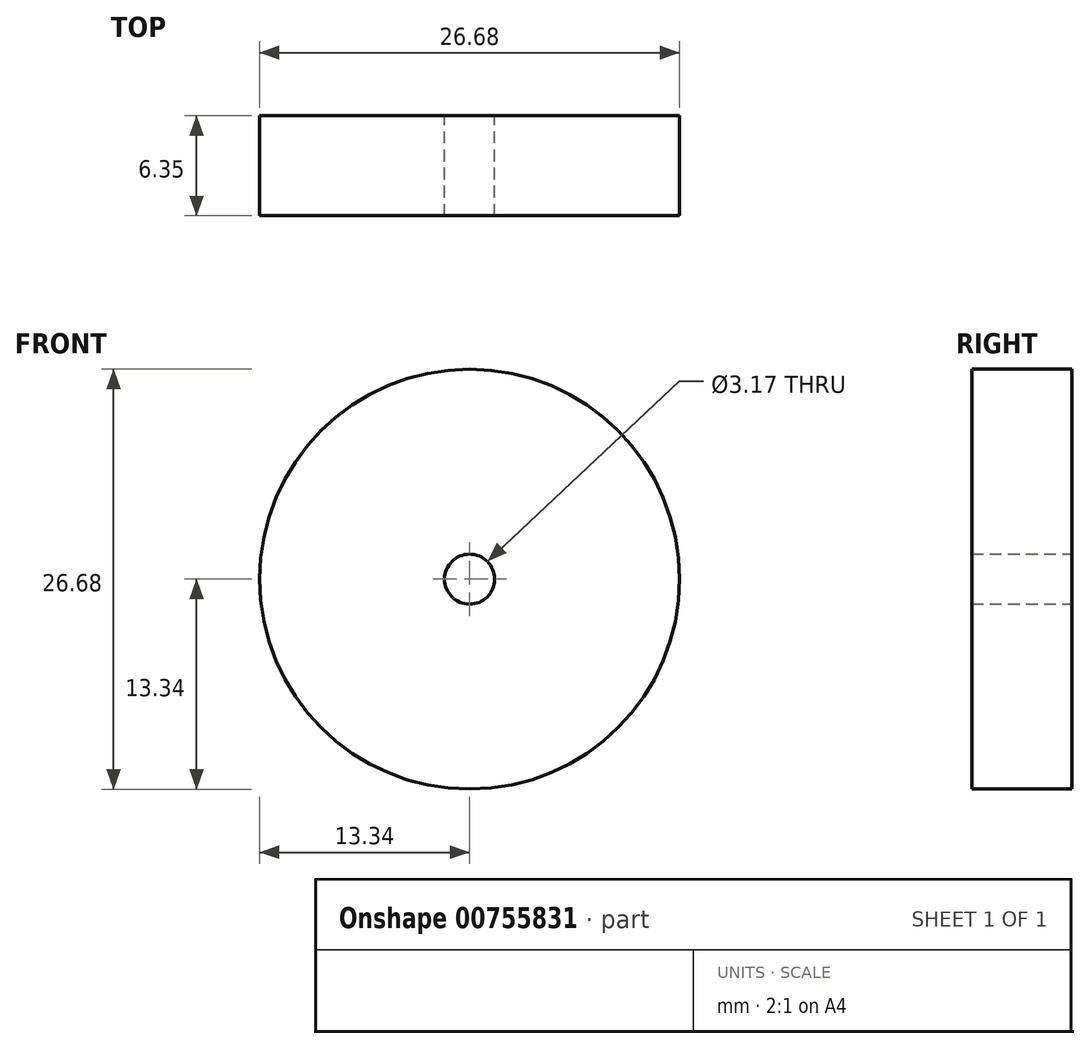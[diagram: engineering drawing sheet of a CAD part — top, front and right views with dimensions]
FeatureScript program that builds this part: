
annotation { "Feature Type Name" : "Feature", "Feature Type Description" : "" }
export const myFeature = defineFeature(function(context is Context, id is Id, definition is map)
    precondition{}
    {
        {
            var Q0;
            Q0=qCreatedBy(makeId("Front.planeOp"),FACE);
            var sketch = newSketch(context, id + "F0", { "sketchPlane" : qUnion([Q0])});
            skCircle(sketch, "E0", {"center": v(0, 0) * mm, "radius": 13.34 * mm});
            skCircle(sketch, "E1", {"center": v(0, 0) * mm, "radius": 1.59 * mm});
            skSolve(sketch);
        }
        {
            var Q0;
            Q0=qSketchRegion(id+"F0",true);
            extrude(context, id + "F1", {"entities" : qUnion([Q0]), "depth" : 6.35 * mm, "offsetDistance" : 25.4 * mm});
        }
    });
